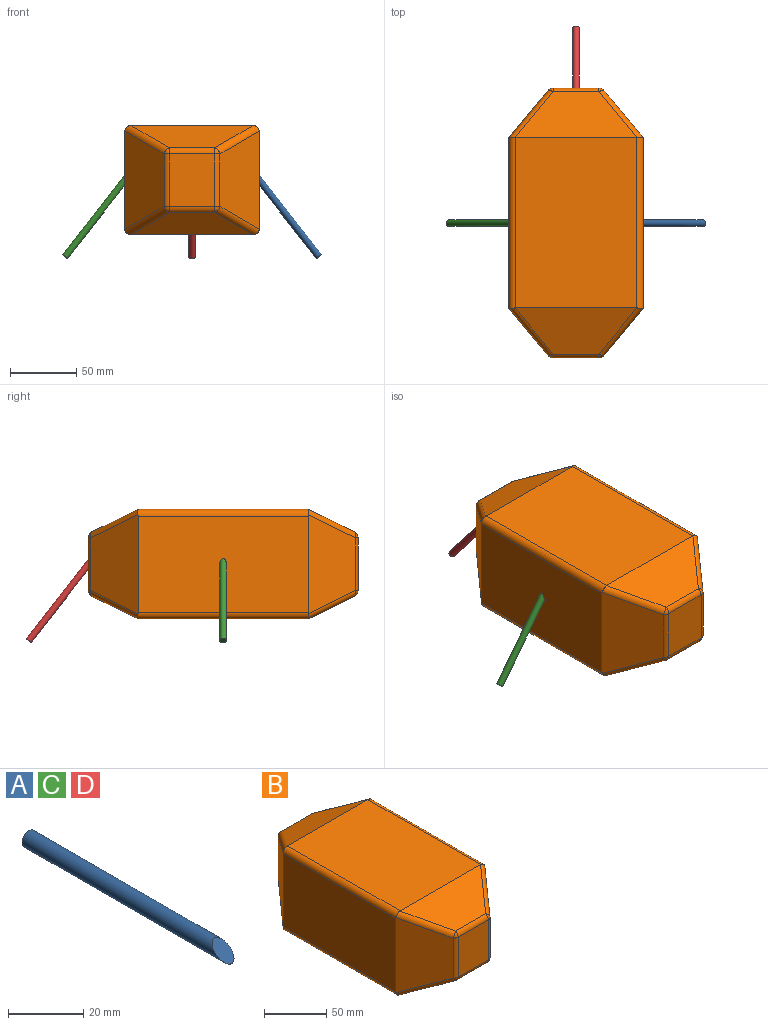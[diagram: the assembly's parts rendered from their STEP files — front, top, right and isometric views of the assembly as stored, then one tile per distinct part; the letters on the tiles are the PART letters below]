
ASSEMBLY  parts=4 mates=3
PART A: 3 faces, bbox 5.1x76.2x5.1 mm
  f0: plane 5.08x5.08mm, normal (0,1,0), area 20.3mm2, adj f1
  f1: cylinder r=2.54mm len=76.24mm, axis (0,1,0), area 1164.1mm2, adj f0,f2
  f2: plane 6.52x5.08mm, normal (0,-0.61,0.79), area 33mm2, adj f1
PART B: 42 faces, bbox 101.7x203.3x83.5 mm
  f0: plane 74.36x35.8mm, normal (-0.77,-0.64,0), area 2648.7mm2, adj f9,f26,f32,f38,f39,f41
  f1: plane 39.52x34.32mm, normal (0,-1,0), area 1356.3mm2, adj f30,f31,f37,f38
  f2: plane 74.36x35.8mm, normal (0.77,-0.64,0), area 2648.7mm2, adj f8,f16,f20,f24,f29,f30
  f3: plane 74.36x35.8mm, normal (0.77,0.64,0), area 2648.7mm2, adj f8,f14,f16,f18,f19,f24
  f4: plane 39.52x34.32mm, normal (0,1,0), area 1356.3mm2, adj f17,f18,f27,f28
  f5: plane 74.36x35.8mm, normal (-0.77,0.64,0), area 2648.7mm2, adj f9,f21,f26,f27,f36,f39
  f6: plane 128.04x91.44mm, normal (0,0,1), area 11708.2mm2, adj f11,f13,f24,f39
  f7: plane 128.04x91.44mm, normal (0,0,-1), area 11708.2mm2, adj f10,f12,f16,f26
  f8: plane 128.04x72.39mm, normal (1,0,0), area 9269mm2, adj f2,f3,f16,f24
  f9: plane 128.04x72.39mm, normal (-1,0,0), area 9269mm2, adj f0,f5,f26,f39
  f10: plane 92.07x34.74mm, normal (0,0.44,-0.9), area 2442.5mm2, adj f7,f14,f16,f17,f21,f26
  f11: plane 92.07x34.74mm, normal (0,0.44,0.9), area 2442.5mm2, adj f6,f19,f24,f28,f36,f39
  f12: plane 92.07x34.74mm, normal (0,-0.44,-0.9), area 2442.5mm2, adj f7,f16,f20,f26,f31,f32
  f13: plane 92.07x34.74mm, normal (0,-0.44,0.9), area 2442.5mm2, adj f6,f24,f29,f37,f39,f41
  f14: cylinder r=5.08mm len=36.96mm, axis (-0.6,0.72,0.35), area 321.4mm2, adj f3,f10,f15,f16
  f15: sphere r=5.08mm, area 14.7mm2, adj f14,f17,f18
  f16: cylinder r=5.08mm len=128.87mm, axis (0,1,0), area 1025.6mm2, adj f2,f3,f7,f8,f10,f12,f14,f20
  f17: cylinder r=5.08mm len=34.32mm, axis (-1,0,0), area 194.7mm2, adj f4,f10,f15,f22
  f18: cylinder r=5.08mm len=39.52mm, axis (0,0,1), area 176.1mm2, adj f3,f4,f15,f23
  f19: cylinder r=5.08mm len=36.96mm, axis (0.6,-0.72,0.35), area 321.4mm2, adj f3,f11,f23,f24
  f20: cylinder r=5.08mm len=36.96mm, axis (0.6,0.72,-0.35), area 321.4mm2, adj f2,f12,f16,f25
  f21: cylinder r=5.08mm len=36.96mm, axis (-0.6,-0.72,-0.35), area 321.4mm2, adj f5,f10,f22,f26
  f22: sphere r=5.08mm, area 14.7mm2, adj f17,f21,f27
  f23: sphere r=5.08mm, area 14.7mm2, adj f18,f19,f28
  f24: cylinder r=5.08mm len=128.87mm, axis (0,-1,0), area 1025.6mm2, adj f2,f3,f6,f8,f11,f13,f19,f29
  f25: sphere r=5.08mm, area 14.7mm2, adj f20,f30,f31
  f26: cylinder r=5.08mm len=128.87mm, axis (0,-1,0), area 1025.6mm2, adj f0,f5,f7,f9,f10,f12,f21,f32
  f27: cylinder r=5.08mm len=39.52mm, axis (0,0,-1), area 176.1mm2, adj f4,f5,f22,f33
  f28: cylinder r=5.08mm len=34.32mm, axis (1,0,0), area 194.7mm2, adj f4,f11,f23,f33
  f29: cylinder r=5.08mm len=36.96mm, axis (-0.6,-0.72,-0.35), area 321.4mm2, adj f2,f13,f24,f34
  f30: cylinder r=5.08mm len=39.52mm, axis (0,0,1), area 176.1mm2, adj f1,f2,f25,f34
  f31: cylinder r=5.08mm len=34.32mm, axis (1,0,0), area 194.7mm2, adj f1,f12,f25,f35
  f32: cylinder r=5.08mm len=36.96mm, axis (0.6,-0.72,0.35), area 321.4mm2, adj f0,f12,f26,f35
  f33: sphere r=5.08mm, area 14.7mm2, adj f27,f28,f36
  f34: sphere r=5.08mm, area 14.7mm2, adj f29,f30,f37
  f35: sphere r=5.08mm, area 14.7mm2, adj f31,f32,f38
  f36: cylinder r=5.08mm len=36.96mm, axis (0.6,0.72,-0.35), area 321.4mm2, adj f5,f11,f33,f39
  f37: cylinder r=5.08mm len=34.32mm, axis (-1,0,0), area 194.7mm2, adj f1,f13,f34,f40
  f38: cylinder r=5.08mm len=39.52mm, axis (0,0,-1), area 176.1mm2, adj f0,f1,f35,f40
  f39: cylinder r=5.08mm len=128.87mm, axis (0,1,0), area 1025.6mm2, adj f0,f5,f6,f9,f11,f13,f36,f41
  f40: sphere r=5.08mm, area 14.7mm2, adj f37,f38,f41
  f41: cylinder r=5.08mm len=36.96mm, axis (-0.6,0.72,0.35), area 321.4mm2, adj f0,f13,f39,f40
PART C: same geometry as A
PART D: same geometry as A
PLACE A rot(axis=(-0.67,-0.67,0.33),143.8deg) t=(33.08,51.78,29.92)mm
PLACE B t=(-33.64,15.23,10.19)mm
PLACE C rot(axis=(-0.67,0.67,-0.33),143.8deg) t=(-102.09,-44.18,29.92)mm
PLACE D rot(axis=(0,-0.9,0.44),180deg) t=(-82.48,122.19,29.92)mm
MATE fastened D.f2 <-> B.f4  axis (0,-1,0) through (-34.5,105.4,51.46)mm
MATE fastened A.f2 <-> B.f8  axis (-1,0,0) through (16.3,3.8,51.46)mm
MATE fastened C.f2 <-> B.f9  axis (1,0,0) through (-85.3,3.8,51.46)mm
